# Revit family: Faucet-Lavatory-Delta-Tesla-T3552LF_WL
name_source: partatom
category: Plumbing Fixtures
revit_build: Autodesk Revit MEP 2012 (Build: 20110916_2132(x64)
units: mm (PartAtom-declared; Revit-internal decimal feet)

## types (1)
- Standard
    Cold Water Radius = 0.5 "
    Cold Water Supply Flow = 0 GPM
    Connection Flow = 0 GPM
    Date Modified = January 5, 2015
    Default Elevation = 48 "
    Description = Tesla Lavatory Faucet Trim, Three Hole
    Equipment Abbreviation = TF
    Family Version = 1.0
    Hot Water Radius = 0.5 "
    Hot Water Supply Flow = 0 GPM
    Manufacturer = Delta Faucet Company
    Model = T3552LF-WL
    Model Disclaimer = Contact Delta Faucet Company for More Information
    Pipe Connection Radius = 0.5 "
    Product Material = Steel - Delta Faucet Company - Stainless
    URL = http://www.deltafaucet.com
    zz Length 1 = 1.89 "

## geometry (parser evidence)
native form markers: Blend x4, Sweep x2
no freeform markers — native parametric forms only
